# Revit family: LCBA92
name_source: partatom
category: Lighting Fixtures
units: mm (PartAtom-declared; Revit-internal decimal feet)

## family parameters
Always vertical = Yes
Cut with Voids When Loaded = No
Host = Ceiling
Light Source = Yes
OmniClass Number = 23.80.70.11.14.17
OmniClass Title = Direct/Indirect
Part Type = Normal
Room Calculation Point = No
Round Connector Dimension = Use Diameter
Shared = No

## types (1)
- LCBA92-LED840K050LUNV
    Apparent Load = 64 VA
    Assembly Code = D5020200
    Color Filter = 16777215
    Description = LED Commercial Basket A
    Dimming Lamp Color Temperature Shift = <None>
    Emit from Line Length = 7' - 8 1/4"
    Housing Finish = Metal - Viscor - White
    Lamp = LED
    Lamp Wattage = 64 VA
    Length = 7' - 8 1/4"
    Lens Finish Bottom = Acrylic - Viscor - White Opal
    Manufacturer = VISIONEERING by VISCOR
    Model = LCBA
    Photometric Web File = LCBA92-LED840K070LUNV.ies
    Tilt Angle = 180.00°
    URL = https://www.viscor.com
    Voltage = 120 V
    Width = 0' - 10 1/4"

## geometry (parser evidence)
native form markers: Sweep x2
no freeform markers — native parametric forms only
